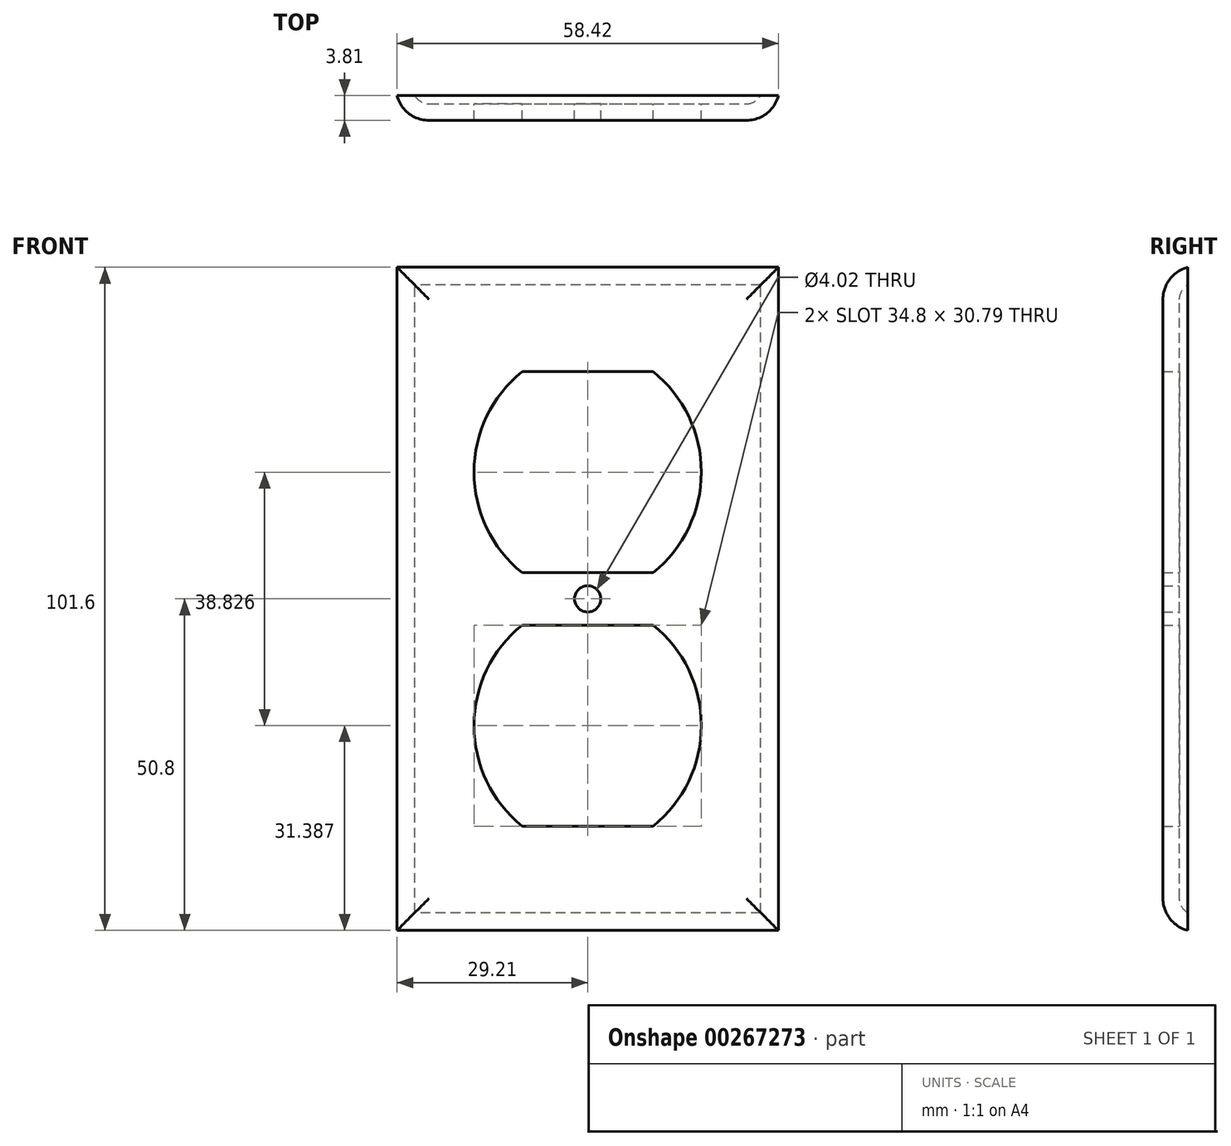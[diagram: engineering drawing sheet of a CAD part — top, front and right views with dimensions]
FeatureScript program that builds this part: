
annotation { "Feature Type Name" : "Feature", "Feature Type Description" : "" }
export const myFeature = defineFeature(function(context is Context, id is Id, definition is map)
    precondition{}
    {
        {
            var Q0;
            Q0=qCreatedBy(makeId("Front.planeOp"),FACE);
            var sketch = newSketch(context, id + "F0", { "sketchPlane" : qUnion([Q0])});
            skLineSegment(sketch, "E0.bottom", {"start": v(29.21, -50.8) * mm, "end": v(-29.2, -50.8) * mm});
            skLineSegment(sketch, "E0.top", {"start": v(29.2, 50.8) * mm, "end": v(-29.2, 50.8) * mm});
            skLineSegment(sketch, "E0.left", {"start": v(29.21, -50.8) * mm, "end": v(29.2, 50.8) * mm});
            skLineSegment(sketch, "E0.right", {"start": v(-29.2, -50.8) * mm, "end": v(-29.21, 50.8) * mm});
            skPoint(sketch, "E1.endSnap0", {"position": v(0, 50.8) * mm});
            skSolve(sketch);
        }
        {
            var Q0;
            Q0=makeQuery(id+"F0.imprint","IMPRINT",FACE,{"disambiguationData":[TD([[makeQuery(id+"F0.imprint","IMPRINT",EDGE,{"derivedFrom":sQuery(id+"F0.wireOp",EDGE,"E0.bottom")}),-1.0]])]});
            extrude(context, id + "F1", {"entities" : qUnion([Q0]), "depth" : 3.8 * mm});
        }
        {
            var Q0;
            Q0=makeQuery(id+"F1.opExtrude","CAP_EDGE",EDGE,{"disambiguationData":[OSD([sQuery(id+"F0.wireOp",EDGE,"E0.right")])],"isStart":false});
            var Q1;
            Q1=makeQuery(id+"F1.opExtrude","CAP_EDGE",EDGE,{"disambiguationData":[OSD([sQuery(id+"F0.wireOp",EDGE,"E0.top")])],"isStart":false});
            var Q2;
            Q2=makeQuery(id+"F1.opExtrude","CAP_EDGE",EDGE,{"disambiguationData":[OSD([sQuery(id+"F0.wireOp",EDGE,"E0.left")])],"isStart":false});
            var Q3;
            Q3=makeQuery(id+"F1.opExtrude","CAP_EDGE",EDGE,{"disambiguationData":[OSD([sQuery(id+"F0.wireOp",EDGE,"E0.bottom")])],"isStart":false});
            fillet(context, id + "F2", {"entities" : qUnion([Q0, Q1, Q2, Q3]), "radius" : 5.08 * mm, "tangentPropagation" : true, "allowEdgeOverflow" : false});
        }
        {
            var Q0;
            Q0=makeQuery(id+"F1.opExtrude","CAP_FACE",FACE,{"disambiguationData":[OSD([sQuery(id+"F0.wireOp",EDGE,"E0.bottom"),sQuery(id+"F0.wireOp",EDGE,"E0.top"),sQuery(id+"F0.wireOp",EDGE,"E0.left"),sQuery(id+"F0.wireOp",EDGE,"E0.right"),sQuery(id+"F0.wireOp",EDGE,"De4dDaXl-E2uk-dTT3-FmmK-YiqVM1brrdih"),sQuery(id+"F0.wireOp",EDGE,"0uOFt2SO-TBqW-OznX-mCH0-Je6DuPuG5zKY"),sQuery(id+"F0.wireOp",EDGE,"A5auENO8-va2M-Xfjn-T0x4-UB3nyT9nOIuZ"),sQuery(id+"F0.wireOp",EDGE,"kH1okF8R-3wtx-xmz0-BiqD-nw23Sz0e4a28"),sQuery(id+"F0.wireOp",EDGE,"c083d653-d649-4963-953d-09737561f69d0.MirrorCS"),sQuery(id+"F0.wireOp",EDGE,"431f43b8-db4e-4c23-bdc1-67874eee7f290.MirrorCS"),sQuery(id+"F0.wireOp",EDGE,"322dafae-9c31-4b18-b13c-738814d3bf7b0.MirrorCS"),sQuery(id+"F0.wireOp",EDGE,"8de16ecb-0e0c-42a2-b15f-c67aa722de1c0.MirrorCS"),sQuery(id+"F0.wireOp",EDGE,"18a3d229-c979-4708-880b-db4fb31e49850.MirrorCS")])],"isStart":true});
            var sketch = newSketch(context, id + "F3", { "sketchPlane" : qUnion([Q0])});
            skLineSegment(sketch, "E2", {"start": v(-10.04, 34.8) * mm, "end": v(10.04, 34.8) * mm});
            skLineSegment(sketch, "E3", {"start": v(-10.04, 4.02) * mm, "end": v(10.04, 4.02) * mm});
            skArc(sketch, "E4", {"start": v(-10.04, 34.8) * mm, "mid": v(-17.4, 19.41) * mm, "end": v(-10.04, 4.02) * mm});
            skArc(sketch, "E5.MirrorCS", {"start": v(10.04, 34.8) * mm, "mid": v(17.4, 19.41) * mm, "end": v(10.04, 4.02) * mm});
            skLineSegment(sketch, "E6.MirrorCS", {"start": v(-10.04, -4.02) * mm, "end": v(10.04, -4.02) * mm});
            skArc(sketch, "E7.MirrorCS", {"start": v(-10.04, -34.8) * mm, "mid": v(-17.4, -19.41) * mm, "end": v(-10.04, -4.02) * mm});
            skLineSegment(sketch, "E8.MirrorCS", {"start": v(-10.04, -34.8) * mm, "end": v(10.04, -34.8) * mm});
            skArc(sketch, "E9.MirrorCS", {"start": v(10.04, -34.8) * mm, "mid": v(17.4, -19.41) * mm, "end": v(10.04, -4.02) * mm});
            skCircle(sketch, "E10", {"center": v(0, 0) * mm, "radius": 2 * mm});
            skSolve(sketch);
        }
        {
            var Q0;
            Q0=makeQuery(id+"F1.opExtrude","CAP_FACE",FACE,{"disambiguationData":[OSD([sQuery(id+"F0.wireOp",EDGE,"E0.bottom"),sQuery(id+"F0.wireOp",EDGE,"E0.top"),sQuery(id+"F0.wireOp",EDGE,"E0.left"),sQuery(id+"F0.wireOp",EDGE,"E0.right"),sQuery(id+"F0.wireOp",EDGE,"De4dDaXl-E2uk-dTT3-FmmK-YiqVM1brrdih"),sQuery(id+"F0.wireOp",EDGE,"0uOFt2SO-TBqW-OznX-mCH0-Je6DuPuG5zKY"),sQuery(id+"F0.wireOp",EDGE,"A5auENO8-va2M-Xfjn-T0x4-UB3nyT9nOIuZ"),sQuery(id+"F0.wireOp",EDGE,"kH1okF8R-3wtx-xmz0-BiqD-nw23Sz0e4a28"),sQuery(id+"F0.wireOp",EDGE,"c083d653-d649-4963-953d-09737561f69d0.MirrorCS"),sQuery(id+"F0.wireOp",EDGE,"431f43b8-db4e-4c23-bdc1-67874eee7f290.MirrorCS"),sQuery(id+"F0.wireOp",EDGE,"322dafae-9c31-4b18-b13c-738814d3bf7b0.MirrorCS"),sQuery(id+"F0.wireOp",EDGE,"8de16ecb-0e0c-42a2-b15f-c67aa722de1c0.MirrorCS"),sQuery(id+"F0.wireOp",EDGE,"18a3d229-c979-4708-880b-db4fb31e49850.MirrorCS")])],"isStart":true});
            shell(context, id + "F4", {"entities" : qUnion([Q0]), "thickness" : 2.54 * mm});
        }
        {
            var Q0;
            Q0 = qSketchRegion(id + "F3", true);
            extrude(context, id + "F5", {"entities" : qUnion([Q0]), "operationType" : NewBodyOperationType.REMOVE, "oppositeDirection" : true, "depth" : 25.4 * mm});
        }
    });
